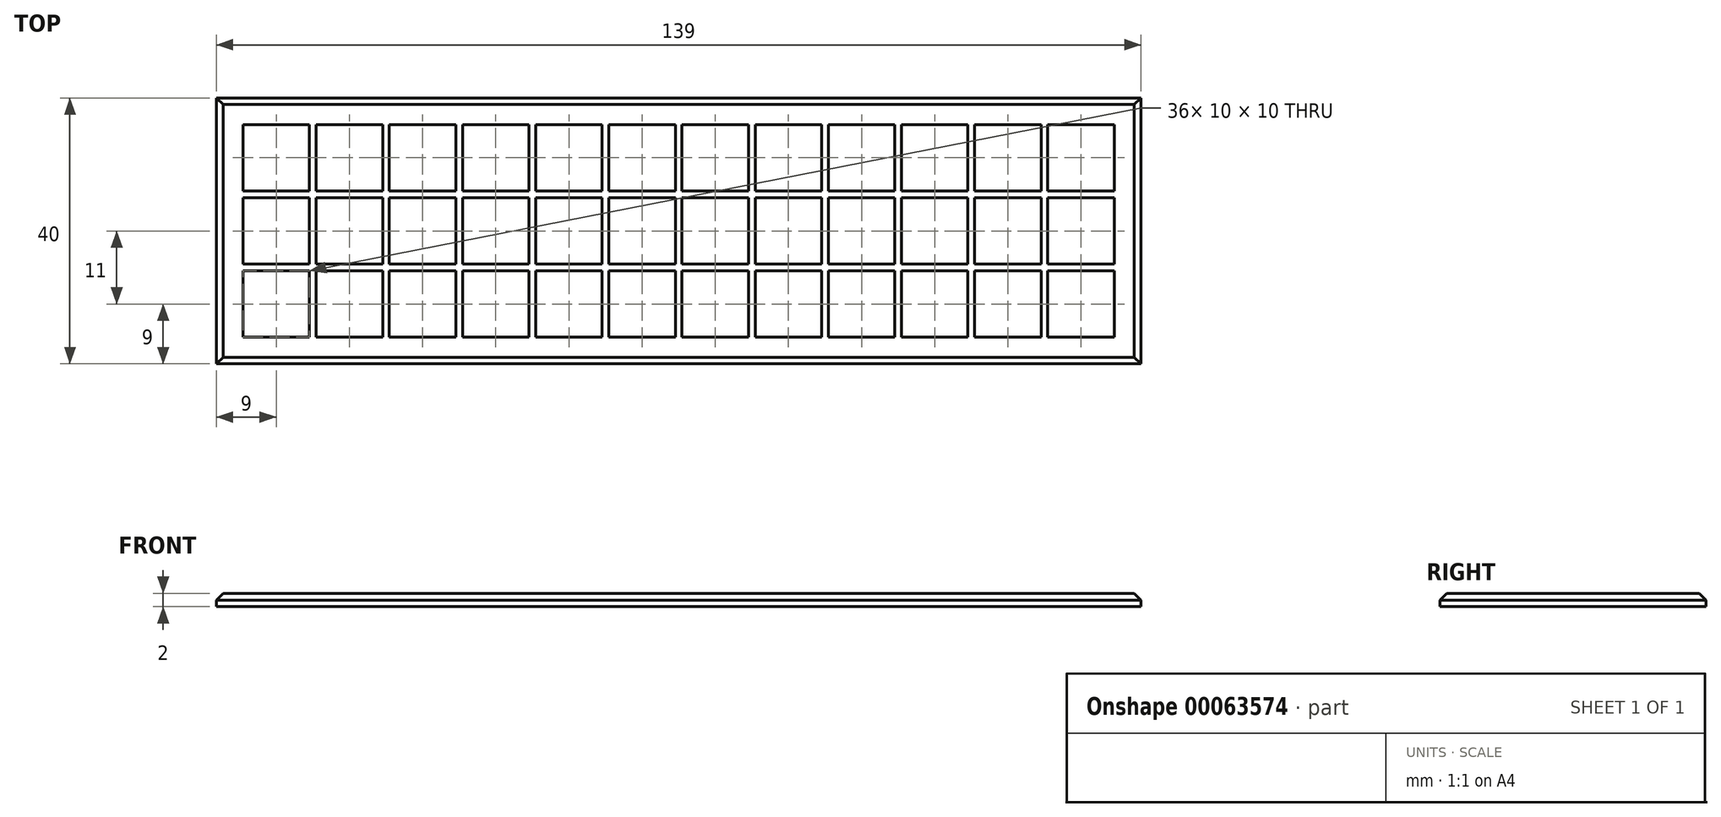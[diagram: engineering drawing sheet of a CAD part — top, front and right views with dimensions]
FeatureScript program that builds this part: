
annotation { "Feature Type Name" : "Feature", "Feature Type Description" : "" }
export const myFeature = defineFeature(function(context is Context, id is Id, definition is map)
    precondition{}
    {
        {
            var Q0;
            Q0=qCreatedBy(makeId("Top.planeOp"),FACE);
            var sketch = newSketch(context, id + "F0", { "sketchPlane" : qUnion([Q0])});
            skLineSegment(sketch, "E0.rect.bottom", {"start": v(5, -5) * mm, "end": v(-5, -5) * mm});
            skLineSegment(sketch, "E0.rect.top", {"start": v(5, 5) * mm, "end": v(-5, 5) * mm});
            skLineSegment(sketch, "E0.rect.left", {"start": v(5, -5) * mm, "end": v(5, 5) * mm});
            skLineSegment(sketch, "E0.rect.right", {"start": v(-5, -5) * mm, "end": v(-5, 5) * mm});
            skPoint(sketch, "E0.rect.middle", {"position": v(0, 0) * mm});
            skLineSegment(sketch, "E1.0.1.0", {"start": v(-5, 6) * mm, "end": v(-5, 16) * mm});
            skLineSegment(sketch, "E1.0.1.1", {"start": v(5, 16) * mm, "end": v(-5, 16) * mm});
            skLineSegment(sketch, "E1.0.1.2", {"start": v(5, 6) * mm, "end": v(5, 16) * mm});
            skLineSegment(sketch, "E1.0.1.3", {"start": v(5, 6) * mm, "end": v(-5, 6) * mm});
            skLineSegment(sketch, "E1.0.2.0", {"start": v(-5, 17) * mm, "end": v(-5, 27) * mm});
            skLineSegment(sketch, "E1.0.2.1", {"start": v(5, 27) * mm, "end": v(-5, 27) * mm});
            skLineSegment(sketch, "E1.0.2.2", {"start": v(5, 17) * mm, "end": v(5, 27) * mm});
            skLineSegment(sketch, "E1.0.2.3", {"start": v(5, 17) * mm, "end": v(-5, 17) * mm});
            skLineSegment(sketch, "E1.1.0.0", {"start": v(6, -5) * mm, "end": v(6, 5) * mm});
            skLineSegment(sketch, "E1.1.0.1", {"start": v(16, 5) * mm, "end": v(6, 5) * mm});
            skLineSegment(sketch, "E1.1.0.2", {"start": v(16, -5) * mm, "end": v(16, 5) * mm});
            skLineSegment(sketch, "E1.1.0.3", {"start": v(16, -5) * mm, "end": v(6, -5) * mm});
            skLineSegment(sketch, "E1.1.1.0", {"start": v(6, 6) * mm, "end": v(6, 16) * mm});
            skLineSegment(sketch, "E1.1.1.1", {"start": v(16, 16) * mm, "end": v(6, 16) * mm});
            skLineSegment(sketch, "E1.1.1.2", {"start": v(16, 6) * mm, "end": v(16, 16) * mm});
            skLineSegment(sketch, "E1.1.1.3", {"start": v(16, 6) * mm, "end": v(6, 6) * mm});
            skLineSegment(sketch, "E1.1.2.0", {"start": v(6, 17) * mm, "end": v(6, 27) * mm});
            skLineSegment(sketch, "E1.1.2.1", {"start": v(16, 27) * mm, "end": v(6, 27) * mm});
            skLineSegment(sketch, "E1.1.2.2", {"start": v(16, 17) * mm, "end": v(16, 27) * mm});
            skLineSegment(sketch, "E1.1.2.3", {"start": v(16, 17) * mm, "end": v(6, 17) * mm});
            skLineSegment(sketch, "E1.2.0.0", {"start": v(17, -5) * mm, "end": v(17, 5) * mm});
            skLineSegment(sketch, "E1.2.0.1", {"start": v(27, 5) * mm, "end": v(17, 5) * mm});
            skLineSegment(sketch, "E1.2.0.2", {"start": v(27, -5) * mm, "end": v(27, 5) * mm});
            skLineSegment(sketch, "E1.2.0.3", {"start": v(27, -5) * mm, "end": v(17, -5) * mm});
            skLineSegment(sketch, "E1.2.1.0", {"start": v(17, 6) * mm, "end": v(17, 16) * mm});
            skLineSegment(sketch, "E1.2.1.1", {"start": v(27, 16) * mm, "end": v(17, 16) * mm});
            skLineSegment(sketch, "E1.2.1.2", {"start": v(27, 6) * mm, "end": v(27, 16) * mm});
            skLineSegment(sketch, "E1.2.1.3", {"start": v(27, 6) * mm, "end": v(17, 6) * mm});
            skLineSegment(sketch, "E1.2.2.0", {"start": v(17, 17) * mm, "end": v(17, 27) * mm});
            skLineSegment(sketch, "E1.2.2.1", {"start": v(27, 27) * mm, "end": v(17, 27) * mm});
            skLineSegment(sketch, "E1.2.2.2", {"start": v(27, 17) * mm, "end": v(27, 27) * mm});
            skLineSegment(sketch, "E1.2.2.3", {"start": v(27, 17) * mm, "end": v(17, 17) * mm});
            skLineSegment(sketch, "E1.3.0.0", {"start": v(28, -5) * mm, "end": v(28, 5) * mm});
            skLineSegment(sketch, "E1.3.0.1", {"start": v(38, 5) * mm, "end": v(28, 5) * mm});
            skLineSegment(sketch, "E1.3.0.2", {"start": v(38, -5) * mm, "end": v(38, 5) * mm});
            skLineSegment(sketch, "E1.3.0.3", {"start": v(38, -5) * mm, "end": v(28, -5) * mm});
            skLineSegment(sketch, "E1.3.1.0", {"start": v(28, 6) * mm, "end": v(28, 16) * mm});
            skLineSegment(sketch, "E1.3.1.1", {"start": v(38, 16) * mm, "end": v(28, 16) * mm});
            skLineSegment(sketch, "E1.3.1.2", {"start": v(38, 6) * mm, "end": v(38, 16) * mm});
            skLineSegment(sketch, "E1.3.1.3", {"start": v(38, 6) * mm, "end": v(28, 6) * mm});
            skLineSegment(sketch, "E1.3.2.0", {"start": v(28, 17) * mm, "end": v(28, 27) * mm});
            skLineSegment(sketch, "E1.3.2.1", {"start": v(38, 27) * mm, "end": v(28, 27) * mm});
            skLineSegment(sketch, "E1.3.2.2", {"start": v(38, 17) * mm, "end": v(38, 27) * mm});
            skLineSegment(sketch, "E1.3.2.3", {"start": v(38, 17) * mm, "end": v(28, 17) * mm});
            skLineSegment(sketch, "E1.4.0.0", {"start": v(39, -5) * mm, "end": v(39, 5) * mm});
            skLineSegment(sketch, "E1.4.0.1", {"start": v(49, 5) * mm, "end": v(39, 5) * mm});
            skLineSegment(sketch, "E1.4.0.2", {"start": v(49, -5) * mm, "end": v(49, 5) * mm});
            skLineSegment(sketch, "E1.4.0.3", {"start": v(49, -5) * mm, "end": v(39, -5) * mm});
            skLineSegment(sketch, "E1.4.1.0", {"start": v(39, 6) * mm, "end": v(39, 16) * mm});
            skLineSegment(sketch, "E1.4.1.1", {"start": v(49, 16) * mm, "end": v(39, 16) * mm});
            skLineSegment(sketch, "E1.4.1.2", {"start": v(49, 6) * mm, "end": v(49, 16) * mm});
            skLineSegment(sketch, "E1.4.1.3", {"start": v(49, 6) * mm, "end": v(39, 6) * mm});
            skLineSegment(sketch, "E1.4.2.0", {"start": v(39, 17) * mm, "end": v(39, 27) * mm});
            skLineSegment(sketch, "E1.4.2.1", {"start": v(49, 27) * mm, "end": v(39, 27) * mm});
            skLineSegment(sketch, "E1.4.2.2", {"start": v(49, 17) * mm, "end": v(49, 27) * mm});
            skLineSegment(sketch, "E1.4.2.3", {"start": v(49, 17) * mm, "end": v(39, 17) * mm});
            skLineSegment(sketch, "E1.5.0.0", {"start": v(50, -5) * mm, "end": v(50, 5) * mm});
            skLineSegment(sketch, "E1.5.0.1", {"start": v(60, 5) * mm, "end": v(50, 5) * mm});
            skLineSegment(sketch, "E1.5.0.2", {"start": v(60, -5) * mm, "end": v(60, 5) * mm});
            skLineSegment(sketch, "E1.5.0.3", {"start": v(60, -5) * mm, "end": v(50, -5) * mm});
            skLineSegment(sketch, "E1.5.1.0", {"start": v(50, 6) * mm, "end": v(50, 16) * mm});
            skLineSegment(sketch, "E1.5.1.1", {"start": v(60, 16) * mm, "end": v(50, 16) * mm});
            skLineSegment(sketch, "E1.5.1.2", {"start": v(60, 6) * mm, "end": v(60, 16) * mm});
            skLineSegment(sketch, "E1.5.1.3", {"start": v(60, 6) * mm, "end": v(50, 6) * mm});
            skLineSegment(sketch, "E1.5.2.0", {"start": v(50, 17) * mm, "end": v(50, 27) * mm});
            skLineSegment(sketch, "E1.5.2.1", {"start": v(60, 27) * mm, "end": v(50, 27) * mm});
            skLineSegment(sketch, "E1.5.2.2", {"start": v(60, 17) * mm, "end": v(60, 27) * mm});
            skLineSegment(sketch, "E1.5.2.3", {"start": v(60, 17) * mm, "end": v(50, 17) * mm});
            skLineSegment(sketch, "E1.6.0.0", {"start": v(61, -5) * mm, "end": v(61, 5) * mm});
            skLineSegment(sketch, "E1.6.0.1", {"start": v(71, 5) * mm, "end": v(61, 5) * mm});
            skLineSegment(sketch, "E1.6.0.2", {"start": v(71, -5) * mm, "end": v(71, 5) * mm});
            skLineSegment(sketch, "E1.6.0.3", {"start": v(71, -5) * mm, "end": v(61, -5) * mm});
            skLineSegment(sketch, "E1.6.1.0", {"start": v(61, 6) * mm, "end": v(61, 16) * mm});
            skLineSegment(sketch, "E1.6.1.1", {"start": v(71, 16) * mm, "end": v(61, 16) * mm});
            skLineSegment(sketch, "E1.6.1.2", {"start": v(71, 6) * mm, "end": v(71, 16) * mm});
            skLineSegment(sketch, "E1.6.1.3", {"start": v(71, 6) * mm, "end": v(61, 6) * mm});
            skLineSegment(sketch, "E1.6.2.0", {"start": v(61, 17) * mm, "end": v(61, 27) * mm});
            skLineSegment(sketch, "E1.6.2.1", {"start": v(71, 27) * mm, "end": v(61, 27) * mm});
            skLineSegment(sketch, "E1.6.2.2", {"start": v(71, 17) * mm, "end": v(71, 27) * mm});
            skLineSegment(sketch, "E1.6.2.3", {"start": v(71, 17) * mm, "end": v(61, 17) * mm});
            skLineSegment(sketch, "E1.7.0.0", {"start": v(72, -5) * mm, "end": v(72, 5) * mm});
            skLineSegment(sketch, "E1.7.0.1", {"start": v(82, 5) * mm, "end": v(72, 5) * mm});
            skLineSegment(sketch, "E1.7.0.2", {"start": v(82, -5) * mm, "end": v(82, 5) * mm});
            skLineSegment(sketch, "E1.7.0.3", {"start": v(82, -5) * mm, "end": v(72, -5) * mm});
            skLineSegment(sketch, "E1.7.1.0", {"start": v(72, 6) * mm, "end": v(72, 16) * mm});
            skLineSegment(sketch, "E1.7.1.1", {"start": v(82, 16) * mm, "end": v(72, 16) * mm});
            skLineSegment(sketch, "E1.7.1.2", {"start": v(82, 6) * mm, "end": v(82, 16) * mm});
            skLineSegment(sketch, "E1.7.1.3", {"start": v(82, 6) * mm, "end": v(72, 6) * mm});
            skLineSegment(sketch, "E1.7.2.0", {"start": v(72, 17) * mm, "end": v(72, 27) * mm});
            skLineSegment(sketch, "E1.7.2.1", {"start": v(82, 27) * mm, "end": v(72, 27) * mm});
            skLineSegment(sketch, "E1.7.2.2", {"start": v(82, 17) * mm, "end": v(82, 27) * mm});
            skLineSegment(sketch, "E1.7.2.3", {"start": v(82, 17) * mm, "end": v(72, 17) * mm});
            skLineSegment(sketch, "E1.8.0.0", {"start": v(83, -5) * mm, "end": v(83, 5) * mm});
            skLineSegment(sketch, "E1.8.0.1", {"start": v(93, 5) * mm, "end": v(83, 5) * mm});
            skLineSegment(sketch, "E1.8.0.2", {"start": v(93, -5) * mm, "end": v(93, 5) * mm});
            skLineSegment(sketch, "E1.8.0.3", {"start": v(93, -5) * mm, "end": v(83, -5) * mm});
            skLineSegment(sketch, "E1.8.1.0", {"start": v(83, 6) * mm, "end": v(83, 16) * mm});
            skLineSegment(sketch, "E1.8.1.1", {"start": v(93, 16) * mm, "end": v(83, 16) * mm});
            skLineSegment(sketch, "E1.8.1.2", {"start": v(93, 6) * mm, "end": v(93, 16) * mm});
            skLineSegment(sketch, "E1.8.1.3", {"start": v(93, 6) * mm, "end": v(83, 6) * mm});
            skLineSegment(sketch, "E1.8.2.0", {"start": v(83, 17) * mm, "end": v(83, 27) * mm});
            skLineSegment(sketch, "E1.8.2.1", {"start": v(93, 27) * mm, "end": v(83, 27) * mm});
            skLineSegment(sketch, "E1.8.2.2", {"start": v(93, 17) * mm, "end": v(93, 27) * mm});
            skLineSegment(sketch, "E1.8.2.3", {"start": v(93, 17) * mm, "end": v(83, 17) * mm});
            skLineSegment(sketch, "E1.9.0.0", {"start": v(94, -5) * mm, "end": v(94, 5) * mm});
            skLineSegment(sketch, "E1.9.0.1", {"start": v(104, 5) * mm, "end": v(94, 5) * mm});
            skLineSegment(sketch, "E1.9.0.2", {"start": v(104, -5) * mm, "end": v(104, 5) * mm});
            skLineSegment(sketch, "E1.9.0.3", {"start": v(104, -5) * mm, "end": v(94, -5) * mm});
            skLineSegment(sketch, "E1.9.1.0", {"start": v(94, 6) * mm, "end": v(94, 16) * mm});
            skLineSegment(sketch, "E1.9.1.1", {"start": v(104, 16) * mm, "end": v(94, 16) * mm});
            skLineSegment(sketch, "E1.9.1.2", {"start": v(104, 6) * mm, "end": v(104, 16) * mm});
            skLineSegment(sketch, "E1.9.1.3", {"start": v(104, 6) * mm, "end": v(94, 6) * mm});
            skLineSegment(sketch, "E1.9.2.0", {"start": v(94, 17) * mm, "end": v(94, 27) * mm});
            skLineSegment(sketch, "E1.9.2.1", {"start": v(104, 27) * mm, "end": v(94, 27) * mm});
            skLineSegment(sketch, "E1.9.2.2", {"start": v(104, 17) * mm, "end": v(104, 27) * mm});
            skLineSegment(sketch, "E1.9.2.3", {"start": v(104, 17) * mm, "end": v(94, 17) * mm});
            skLineSegment(sketch, "E1.10.0.0", {"start": v(105, -5) * mm, "end": v(105, 5) * mm});
            skLineSegment(sketch, "E1.10.0.1", {"start": v(115, 5) * mm, "end": v(105, 5) * mm});
            skLineSegment(sketch, "E1.10.0.2", {"start": v(115, -5) * mm, "end": v(115, 5) * mm});
            skLineSegment(sketch, "E1.10.0.3", {"start": v(115, -5) * mm, "end": v(105, -5) * mm});
            skLineSegment(sketch, "E1.10.1.0", {"start": v(105, 6) * mm, "end": v(105, 16) * mm});
            skLineSegment(sketch, "E1.10.1.1", {"start": v(115, 16) * mm, "end": v(105, 16) * mm});
            skLineSegment(sketch, "E1.10.1.2", {"start": v(115, 6) * mm, "end": v(115, 16) * mm});
            skLineSegment(sketch, "E1.10.1.3", {"start": v(115, 6) * mm, "end": v(105, 6) * mm});
            skLineSegment(sketch, "E1.10.2.0", {"start": v(105, 17) * mm, "end": v(105, 27) * mm});
            skLineSegment(sketch, "E1.10.2.1", {"start": v(115, 27) * mm, "end": v(105, 27) * mm});
            skLineSegment(sketch, "E1.10.2.2", {"start": v(115, 17) * mm, "end": v(115, 27) * mm});
            skLineSegment(sketch, "E1.10.2.3", {"start": v(115, 17) * mm, "end": v(105, 17) * mm});
            skLineSegment(sketch, "E1.11.0.0", {"start": v(116, -5) * mm, "end": v(116, 5) * mm});
            skLineSegment(sketch, "E1.11.0.1", {"start": v(126, 5) * mm, "end": v(116, 5) * mm});
            skLineSegment(sketch, "E1.11.0.2", {"start": v(126, -5) * mm, "end": v(126, 5) * mm});
            skLineSegment(sketch, "E1.11.0.3", {"start": v(126, -5) * mm, "end": v(116, -5) * mm});
            skLineSegment(sketch, "E1.11.1.0", {"start": v(116, 6) * mm, "end": v(116, 16) * mm});
            skLineSegment(sketch, "E1.11.1.1", {"start": v(126, 16) * mm, "end": v(116, 16) * mm});
            skLineSegment(sketch, "E1.11.1.2", {"start": v(126, 6) * mm, "end": v(126, 16) * mm});
            skLineSegment(sketch, "E1.11.1.3", {"start": v(126, 6) * mm, "end": v(116, 6) * mm});
            skLineSegment(sketch, "E1.11.2.0", {"start": v(116, 17) * mm, "end": v(116, 27) * mm});
            skLineSegment(sketch, "E1.11.2.1", {"start": v(126, 27) * mm, "end": v(116, 27) * mm});
            skLineSegment(sketch, "E1.11.2.2", {"start": v(126, 17) * mm, "end": v(126, 27) * mm});
            skLineSegment(sketch, "E1.11.2.3", {"start": v(126, 17) * mm, "end": v(116, 17) * mm});
            skLineSegment(sketch, "E1.direction1", {"start": v(-5, -5) * mm, "end": v(6, -5) * mm, "construction": true});
            skLineSegment(sketch, "E1.direction2", {"start": v(-5, -5) * mm, "end": v(-5, 6) * mm, "construction": true});
            skLineSegment(sketch, "E2", {"start": v(-5, -5) * mm, "end": v(126, 27) * mm, "construction": true});
            skLineSegment(sketch, "E3.rect.bottom", {"start": v(-9, 31) * mm, "end": v(130, 31) * mm});
            skLineSegment(sketch, "E3.rect.top", {"start": v(-9, -9) * mm, "end": v(130, -9) * mm});
            skLineSegment(sketch, "E3.rect.left", {"start": v(-9, 31) * mm, "end": v(-9, -9) * mm});
            skLineSegment(sketch, "E3.rect.right", {"start": v(130, 31) * mm, "end": v(130, -9) * mm});
            skLineSegment(sketch, "E4", {"start": v(-5, -5) * mm, "end": v(-5, -9) * mm, "construction": true});
            skLineSegment(sketch, "E5", {"start": v(-5, -5) * mm, "end": v(-9, -5) * mm, "construction": true});
            skSolve(sketch);
        }
        {
            var Q0;
            Q0 = qSketchRegion(id + "F0", true);
            extrude(context, id + "F1", {"entities" : qUnion([Q0]), "depth" : 2 * mm});
        }
        {
            var Q0;
            Q0=makeQuery(id+"F1.opExtrude","CAP_EDGE",EDGE,{"disambiguationData":[OSD([sQuery(id+"F0.wireOp",EDGE,"E3.rect.top")])],"isStart":false});
            var Q1;
            Q1=makeQuery(id+"F1.opExtrude","CAP_EDGE",EDGE,{"disambiguationData":[OSD([sQuery(id+"F0.wireOp",EDGE,"E3.rect.left")])],"isStart":false});
            var Q2;
            Q2=makeQuery(id+"F1.opExtrude","CAP_EDGE",EDGE,{"disambiguationData":[OSD([sQuery(id+"F0.wireOp",EDGE,"E3.rect.bottom")])],"isStart":false});
            var Q3;
            Q3=makeQuery(id+"F1.opExtrude","CAP_EDGE",EDGE,{"disambiguationData":[OSD([sQuery(id+"F0.wireOp",EDGE,"E3.rect.right")])],"isStart":false});
            chamfer(context, id + "F2", {"entities" : qUnion([Q0, Q1, Q2, Q3]), "width" : 1 * mm, "tangentPropagation" : true});
        }
    });
